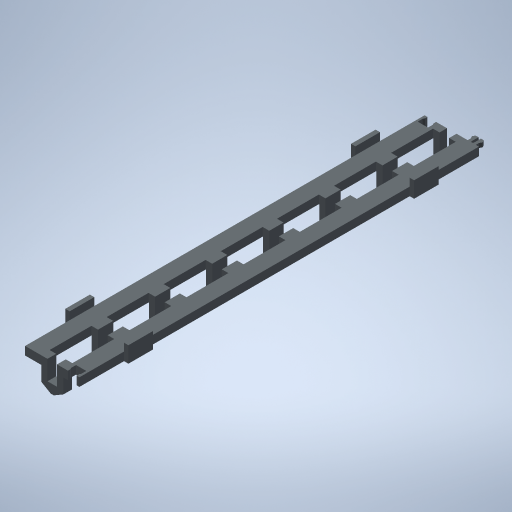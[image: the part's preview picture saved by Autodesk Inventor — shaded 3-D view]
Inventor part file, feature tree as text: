
AUTODESK INVENTOR PART (.ipt)
format: ipt  version: 2023 (Build 270158000, 158)  size: 422,912 bytes
history: native  units: mm
features: extrude x15, sketch x15, other x7
ambient origin geometry x8: Origin, YZ Plane, XZ Plane, XY Plane, X Axis, Y Axis, Z Axis, Center Point
bodies: Solid1 (feature_tree)
feature tree (37):
  extrude  "Extrusion1"  Depth=25.0mm TaperAngle=0.0deg
  extrude  "Extrusion2"  Depth=25.0mm TaperAngle=0.0deg
  extrude  "Extrusion3"  Depth=25.0mm TaperAngle=0.0deg
  extrude  "Extrusion4"  Depth=25.0mm TaperAngle=0.0deg
  extrude  "Extrusion5"  Depth=6.0mm TaperAngle=0.0deg
  extrude  "Extrusion6"  Depth=2.75mm TaperAngle=0.0deg
  extrude  "Extrusion7"  Depth=15.4mm TaperAngle=0.0deg
  extrude  "Extrusion8"  TaperAngle=0.0deg  [1 undecoded]
  extrude  "Extrusion9"  [1 undecoded]
  extrude  "Extrusion11"  [1 undecoded]
  extrude  "Extrusion12"  [1 undecoded]
  extrude  "Extrusion13"  [1 undecoded]
  extrude  "Extrusion14"  [1 undecoded]
  extrude  "Extrusion15"  [1 undecoded]
  extrude  "Extrusion16"  [1 undecoded]
  other  "p1_XY"
  other  "p1_YZ"
  other  "p1_ZX"
  other  "p1_X"
  other  "p1_Y"
  other  "p1_Z"
  other  "p1_Center"
  sketch  "Sketch_1"  dims[d0=250.0mm d1=0.0mm d2=25.0mm d3=0.0mm]
  sketch  "Sketch_9"  dims[d30=15.4mm d31=0.0mm d32=0.0mm]
  sketch  "Sketch_2"  dims[d4=25.0mm d5=0.0mm d6=25.0mm d7=0.0mm]
  sketch  "Sketch_3"  dims[d8=25.0mm d9=0.0mm d10=25.0mm d11=0.0mm]
  sketch  "Sketch_4"  dims[d12=25.0mm d13=0.0mm d14=25.0mm d15=0.0mm]
  sketch  "Sketch_5"  dims[d16=2.7mm d17=0.0mm d20=6.0mm d21=0.0mm]
  sketch  "Sketch_6"  dims[d22=6.0mm d23=0.0mm d24=2.75mm d25=0.0mm]
  sketch  "Sketch_7"  dims[d26=2.75mm d27=0.0mm d28=15.4mm d29=0.0mm]
  sketch  "Sketch_10"
  sketch  "Sketch_12"
  sketch  "Sketch_13"
  sketch  "Sketch_16"
  sketch  "Sketch_14"
  sketch  "Sketch_15"
  sketch  "Sketch_17"
note: 8 required parameter values undecoded (feature->parameter linkage not recoverable at this tier; creation-order binding heuristic only, values carry confidence <= 0.55)
